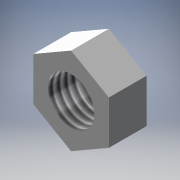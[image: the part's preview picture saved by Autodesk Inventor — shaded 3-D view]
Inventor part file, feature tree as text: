
AUTODESK INVENTOR PART (.ipt)
format: ipt  version: 2016 (Build 200138000, 138)  size: 101,376 bytes
history: native  units: mm
features: extrude x1, thread x1, sketch x1
ambient origin geometry x8: Origin, YZ Plane, XZ Plane, XY Plane, X Axis, Y Axis, Z Axis, Center Point
bodies: Solid1 (feature_tree)
feature tree (3):
  extrude  "Extrusion1"  Depth=10.0mm
  thread  "Thread1"  [1 undecoded]
  sketch  "Sketch1"  dims[d0=13.0mm d1=8.0mm d2=6.5mm d3=0.0mm d4=10.0mm d5=0.0mm]
note: 1 required parameter value undecoded (feature->parameter linkage not recoverable at this tier; creation-order binding heuristic only, values carry confidence <= 0.55)
